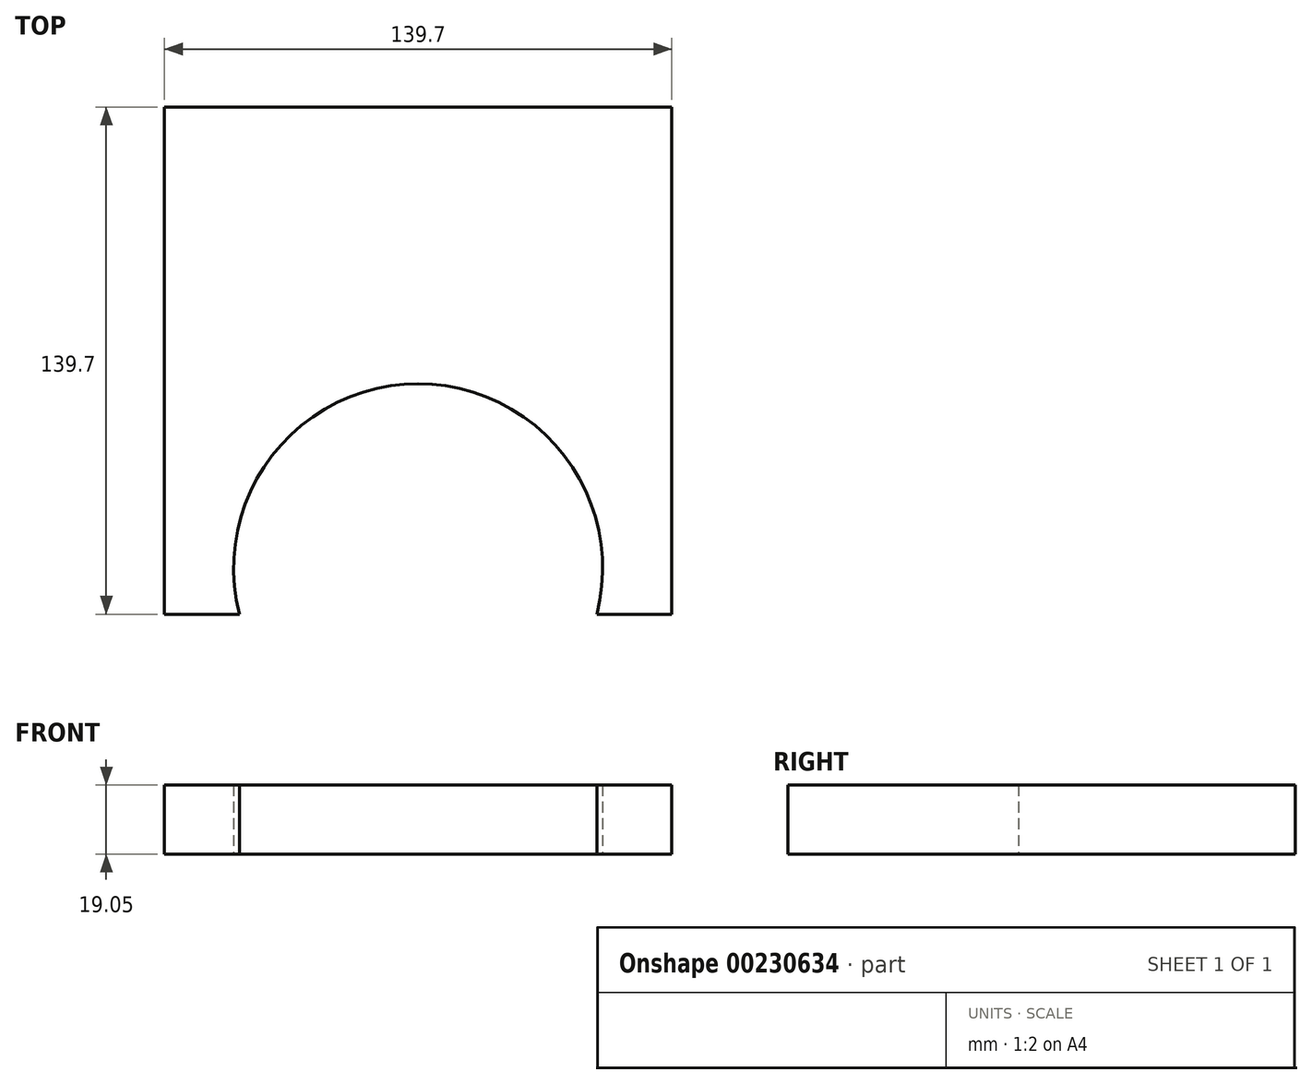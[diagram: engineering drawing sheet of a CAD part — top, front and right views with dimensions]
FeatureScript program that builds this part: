
annotation { "Feature Type Name" : "Feature", "Feature Type Description" : "" }
export const myFeature = defineFeature(function(context is Context, id is Id, definition is map)
    precondition{}
    {
        {
            var Q0;
            Q0=qCreatedBy(makeId("Top.planeOp"),FACE);
            var sketch = newSketch(context, id + "F0", { "sketchPlane" : qUnion([Q0])});
            skLineSegment(sketch, "E0.bottom", {"start": v(69.85, 69.85) * mm, "end": v(-69.85, 69.85) * mm});
            skLineSegment(sketch, "E0.top", {"start": v(69.85, -69.85) * mm, "end": v(49.19, -69.85) * mm});
            skLineSegment(sketch, "E0.left", {"start": v(69.85, 69.85) * mm, "end": v(69.85, -69.85) * mm});
            skLineSegment(sketch, "E0.right", {"start": v(-69.85, 69.85) * mm, "end": v(-69.85, -69.85) * mm});
            skPoint(sketch, "E0.middle", {"position": v(0, 0) * mm});
            skPoint(sketch, "E1.endSnap0", {"position": v(0, -69.85) * mm});
            skArc(sketch, "E2", {"start": v(49.19, -69.85) * mm, "mid": v(0, -6.35) * mm, "end": v(-49.19, -69.85) * mm});
            skLineSegment(sketch, "E3.trimOffspring", {"start": v(-49.19, -69.85) * mm, "end": v(-69.85, -69.85) * mm});
            skPoint(sketch, "E1.start.orphan", {"position": v(0, -69.85) * mm});
            skSolve(sketch);
        }
        {
            var Q0;
            Q0 = qSketchRegion(id + "F0", true);
            extrude(context, id + "F1", {"entities" : qUnion([Q0]), "depth" : 19.05 * mm});
        }
    });
